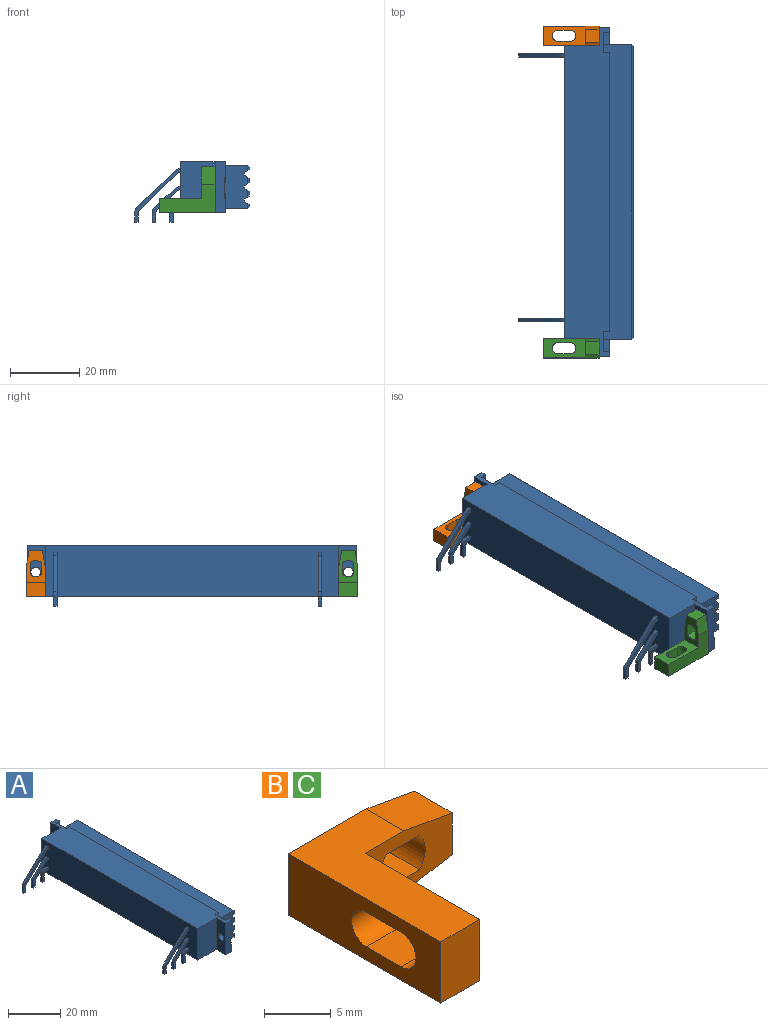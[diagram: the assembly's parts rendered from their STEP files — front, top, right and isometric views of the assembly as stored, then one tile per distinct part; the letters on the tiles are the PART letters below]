
ASSEMBLY  parts=3 mates=6
PART A: 168 faces, bbox 33.1x94.8x17.6 mm
  f0: cylinder r=0.85mm len=1mm, axis (0,-1,0), area 1.3mm2, adj f1,f6,f7,f8
  f1: plane 3.75x1mm, normal (1,0,0), area 3.7mm2, adj f0,f2,f6,f8
  f2: plane 1x1mm, normal (0,0,-1), area 1mm2, adj f1,f3,f6,f8
  f3: plane 3.75x1mm, normal (-1,0,0), area 3.7mm2, adj f2,f4,f6,f8
  f4: cylinder r=1.85mm len=1.85mm, axis (0,-1,0), area 2.9mm2, adj f3,f5,f6,f8
  f5: plane 1.15x1mm, normal (0,0,1), area 1.2mm2, adj f4,f6,f8,f166
  f6: plane 5.6x3mm, normal (0,-1,0), area 7mm2, adj f0,f1,f2,f3,f4,f5,f7,f166
  f7: plane 1.15x1mm, normal (0,0,-1), area 1.2mm2, adj f0,f6,f8,f166
  f8: plane 5.6x3mm, normal (0,1,0), area 7mm2, adj f0,f1,f2,f3,f4,f5,f7,f166
  f9: plane 5.72x5.34mm, normal (0.68,0,-0.73), area 7.8mm2, adj f10,f17,f18,f19
  f10: cylinder r=1mm len=1mm, axis (0,-1,0), area 0.8mm2, adj f9,f11,f17,f19
  f11: plane 2.8x1mm, normal (1,0,0), area 2.8mm2, adj f10,f12,f17,f19
  f12: plane 1x1mm, normal (0,0,-1), area 1mm2, adj f11,f13,f17,f19
  f13: plane 2.8x1mm, normal (-1,0,0), area 2.8mm2, adj f12,f14,f17,f19
  f14: cylinder r=2mm len=1.46mm, axis (0,-1,0), area 1.6mm2, adj f13,f15,f17,f19
  f15: plane 5.72x5.34mm, normal (-0.68,0,0.73), area 7.8mm2, adj f14,f16,f17,f19
  f16: cylinder r=4mm len=1.73mm, axis (0,-1,0), area 2mm2, adj f15,f17,f19,f166
  f17: plane 10.55x8.08mm, normal (0,-1,0), area 13.5mm2, adj f9,f10,f11,f12,f13,f14,f15,f16
  f18: cylinder r=3mm len=1.05mm, axis (0,-1,0), area 1.2mm2, adj f9,f17,f19,f166
  f19: plane 10.55x8.08mm, normal (0,1,0), area 13.5mm2, adj f9,f10,f11,f12,f13,f14,f15,f16
  f20: plane 10.77x10.39mm, normal (0.69,0,-0.72), area 15mm2, adj f21,f28,f29,f30
  f21: cylinder r=1mm len=1mm, axis (0,-1,0), area 0.8mm2, adj f20,f22,f28,f30
  f22: plane 2.8x1mm, normal (1,0,0), area 2.8mm2, adj f21,f23,f28,f30
  f23: plane 1x1mm, normal (0,0,-1), area 1mm2, adj f22,f24,f28,f30
  f24: plane 2.8x1mm, normal (-1,0,0), area 2.8mm2, adj f23,f25,f28,f30
  f25: cylinder r=2mm len=1.44mm, axis (0,-1,0), area 1.6mm2, adj f24,f26,f28,f30
  f26: plane 10.77x10.39mm, normal (-0.69,0,0.72), area 15mm2, adj f25,f27,f28,f30
  f27: cylinder r=4mm len=1.78mm, axis (0,-1,0), area 2.1mm2, adj f26,f28,f30,f166
  f28: plane 15.63x13.16mm, normal (0,-1,0), area 20.6mm2, adj f20,f21,f22,f23,f24,f25,f26,f27
  f29: cylinder r=3mm len=1.08mm, axis (0,-1,0), area 1.3mm2, adj f20,f28,f30,f166
  f30: plane 15.63x13.16mm, normal (0,1,0), area 20.6mm2, adj f20,f21,f22,f23,f24,f25,f26,f27
  f31: cylinder r=0.85mm len=1mm, axis (0,-1,0), area 1.3mm2, adj f32,f37,f38,f39
  f32: plane 3.75x1mm, normal (1,0,0), area 3.7mm2, adj f31,f33,f37,f39
  f33: plane 1x1mm, normal (0,0,-1), area 1mm2, adj f32,f34,f37,f39
  f34: plane 3.75x1mm, normal (-1,0,0), area 3.7mm2, adj f33,f35,f37,f39
  f35: cylinder r=1.85mm len=1.85mm, axis (0,-1,0), area 2.9mm2, adj f34,f36,f37,f39
  f36: plane 1.15x1mm, normal (0,0,1), area 1.1mm2, adj f35,f37,f39,f166
  f37: plane 5.6x3mm, normal (0,-1,0), area 7mm2, adj f31,f32,f33,f34,f35,f36,f38,f166
  f38: plane 1.15x1mm, normal (0,0,-1), area 1.1mm2, adj f31,f37,f39,f166
  f39: plane 5.6x3mm, normal (0,1,0), area 7mm2, adj f31,f32,f33,f34,f35,f36,f38,f166
  f40: plane 5.72x5.34mm, normal (0.68,0,-0.73), area 7.8mm2, adj f41,f48,f49,f50
  f41: cylinder r=1mm len=1mm, axis (0,-1,0), area 0.8mm2, adj f40,f42,f48,f50
  f42: plane 2.8x1mm, normal (1,0,0), area 2.8mm2, adj f41,f43,f48,f50
  f43: plane 1x1mm, normal (0,0,-1), area 1mm2, adj f42,f44,f48,f50
  f44: plane 2.8x1mm, normal (-1,0,0), area 2.8mm2, adj f43,f45,f48,f50
  f45: cylinder r=2mm len=1.46mm, axis (0,-1,0), area 1.6mm2, adj f44,f46,f48,f50
  f46: plane 5.72x5.34mm, normal (-0.68,0,0.73), area 7.8mm2, adj f45,f47,f48,f50
  f47: cylinder r=4mm len=1.73mm, axis (0,-1,0), area 2mm2, adj f46,f48,f50,f166
  f48: plane 10.55x8.08mm, normal (0,-1,0), area 13.5mm2, adj f40,f41,f42,f43,f44,f45,f46,f47
  f49: cylinder r=3mm len=1.05mm, axis (0,-1,0), area 1.2mm2, adj f40,f48,f50,f166
  f50: plane 10.55x8.08mm, normal (0,1,0), area 13.5mm2, adj f40,f41,f42,f43,f44,f45,f46,f47
  f51: cylinder r=1mm len=1mm, axis (0,-1,0), area 0.8mm2, adj f52,f58,f59,f60
  f52: plane 2.8x1mm, normal (1,0,0), area 2.8mm2, adj f51,f53,f58,f60
  f53: plane 1x1mm, normal (0,0,-1), area 1mm2, adj f52,f54,f58,f60
  f54: plane 2.8x1mm, normal (-1,0,0), area 2.8mm2, adj f53,f55,f58,f60
  f55: cylinder r=2mm len=1.44mm, axis (0,-1,0), area 1.6mm2, adj f54,f56,f58,f60
  f56: plane 10.77x10.39mm, normal (-0.69,0,0.72), area 15mm2, adj f55,f57,f58,f60
  f57: cylinder r=4mm len=1.78mm, axis (0,-1,0), area 2.1mm2, adj f56,f58,f60,f166
  f58: plane 15.63x13.16mm, normal (0,-1,0), area 20.6mm2, adj f51,f52,f53,f54,f55,f56,f57,f59
  f59: plane 10.77x10.39mm, normal (0.69,0,-0.72), area 15mm2, adj f51,f58,f60,f167
  f60: plane 15.63x13.16mm, normal (0,1,0), area 20.6mm2, adj f51,f52,f53,f54,f55,f56,f57,f59
  f61: cylinder r=1.4mm len=2.8mm, axis (-1,0,0), area 22.9mm2, adj f63,f157
  f62: plane 14.75x10mm, normal (0,1,0), area 147.5mm2, adj f63,f154,f164,f166
  f63: plane 14.75x5.15mm, normal (-1,0,0), area 69.8mm2, adj f61,f62,f154,f158,f164
  f64: plane 14.75x5.15mm, normal (-1,0,0), area 69.8mm2, adj f65,f143,f154,f164,f165
  f65: cylinder r=1.4mm len=2.8mm, axis (-1,0,0), area 22.9mm2, adj f64,f142
  f66: plane 2.98x1.75mm, normal (0,-1,0), area 5.2mm2, adj f67,f153,f154,f155
  f67: plane 3.45x1.75mm, normal (0,0,1), area 6mm2, adj f66,f129,f153,f155
  f68: plane 2.55x1.47mm, normal (0,0.5,-0.87), area 1.2mm2, adj f129,f155,f156,f157
  f69: plane 3.45x1.75mm, normal (0,0,-1), area 6mm2, adj f129,f161,f162,f163
  f70: plane 2.3x0.8mm, normal (1,0,0), area 1.8mm2, adj f71,f76,f77,f78
  f71: plane 2.3x0.4mm, normal (0,0,1), area 0.9mm2, adj f70,f76,f78,f120
  f72: plane 2.3x0.8mm, normal (1,0,0), area 1.8mm2, adj f73,f74,f121,f122
  f73: plane 2.3x0.4mm, normal (0,0,-1), area 0.9mm2, adj f72,f74,f122,f127
  f74: plane 0.8x0.4mm, normal (0,-1,0), area 0.3mm2, adj f72,f73,f75,f121
  f75: plane 73.9x0.8mm, normal (1,0,0), area 59.1mm2, adj f74,f76,f120,f127
  f76: plane 0.8x0.4mm, normal (0,1,0), area 0.3mm2, adj f70,f71,f75,f77
  f77: plane 2.3x0.4mm, normal (0,0,-1), area 0.9mm2, adj f70,f76,f78,f127
  f78: plane 0.8x0.4mm, normal (0,-1,0), area 0.3mm2, adj f70,f71,f77,f79
  f79: plane 1.93x0.8mm, normal (1,0,0), area 1.5mm2, adj f78,f120,f127,f129
  f80: plane 83.9x1.31mm, normal (1,0,0), area 109.9mm2, adj f81,f118,f119,f120
  f81: plane 1.89x0.5mm, normal (0.71,0.71,0), area 1.1mm2, adj f80,f118,f120,f129
  f82: plane 2.3x0.8mm, normal (1,0,0), area 1.8mm2, adj f83,f88,f89,f90
  f83: plane 2.3x0.4mm, normal (0,0,1), area 0.9mm2, adj f82,f88,f90,f114
  f84: plane 2.3x0.8mm, normal (1,0,0), area 1.8mm2, adj f85,f86,f115,f116
  f85: plane 2.3x0.4mm, normal (0,0,-1), area 0.9mm2, adj f84,f86,f116,f118
  f86: plane 0.8x0.4mm, normal (0,-1,0), area 0.3mm2, adj f84,f85,f87,f115
  f87: plane 73.9x0.8mm, normal (1,0,0), area 59.1mm2, adj f86,f88,f114,f118
  f88: plane 0.8x0.4mm, normal (0,1,0), area 0.3mm2, adj f82,f83,f87,f89
  f89: plane 2.3x0.4mm, normal (0,0,-1), area 0.9mm2, adj f82,f88,f90,f118
  f90: plane 0.8x0.4mm, normal (0,-1,0), area 0.3mm2, adj f82,f83,f89,f91
  f91: plane 1.93x0.8mm, normal (1,0,0), area 1.5mm2, adj f90,f114,f118,f129
  f92: plane 83.9x1.31mm, normal (1,0,0), area 109.9mm2, adj f93,f112,f113,f114
  f93: plane 1.89x0.5mm, normal (0.71,0.71,0), area 1.1mm2, adj f92,f112,f114,f129
  f94: plane 2.3x0.8mm, normal (1,0,0), area 1.8mm2, adj f95,f100,f101,f102
  f95: plane 2.3x0.4mm, normal (0,0,1), area 0.9mm2, adj f94,f100,f102,f108
  f96: plane 2.3x0.8mm, normal (1,0,0), area 1.8mm2, adj f97,f98,f109,f110
  f97: plane 2.3x0.4mm, normal (0,0,-1), area 0.9mm2, adj f96,f98,f110,f112
  f98: plane 0.8x0.4mm, normal (0,-1,0), area 0.3mm2, adj f96,f97,f99,f109
  f99: plane 73.9x0.8mm, normal (1,0,0), area 59.1mm2, adj f98,f100,f108,f112
  f100: plane 0.8x0.4mm, normal (0,1,0), area 0.3mm2, adj f94,f95,f99,f101
  f101: plane 2.3x0.4mm, normal (0,0,-1), area 0.9mm2, adj f94,f100,f102,f112
  f102: plane 0.8x0.4mm, normal (0,-1,0), area 0.3mm2, adj f94,f95,f101,f103
  f103: plane 1.93x0.8mm, normal (1,0,0), area 1.5mm2, adj f102,f108,f112,f129
  f104: plane 83.9x0.64mm, normal (1,0,0), area 53.7mm2, adj f105,f106,f107,f108
  f105: plane 1.43x0.5mm, normal (0.71,0.71,0), area 0.7mm2, adj f104,f106,f108,f129
  f106: plane 84.9x0.5mm, normal (0.71,0,-0.71), area 59.7mm2, adj f104,f105,f107,f130
  f107: plane 1.43x0.5mm, normal (0.71,-0.71,0), area 0.7mm2, adj f104,f106,f108,f141
  f108: plane 84.9x1.47mm, normal (0.5,0,0.87), area 144mm2, adj f95,f99,f103,f104,f105,f107,f109,f111
  f109: plane 2.3x0.4mm, normal (0,0,1), area 0.9mm2, adj f96,f98,f108,f110
  f110: plane 0.8x0.4mm, normal (0,1,0), area 0.3mm2, adj f96,f97,f109,f111
  f111: plane 4.47x0.8mm, normal (1,0,0), area 3.6mm2, adj f108,f110,f112,f141
  f112: plane 84.9x1.47mm, normal (0.5,0,-0.87), area 144mm2, adj f92,f93,f97,f99,f101,f103,f111,f113
  f113: plane 1.89x0.5mm, normal (0.71,-0.71,0), area 1.1mm2, adj f92,f112,f114,f141
  f114: plane 84.9x1.47mm, normal (0.5,0,0.87), area 144mm2, adj f83,f87,f91,f92,f93,f113,f115,f117
  f115: plane 2.3x0.4mm, normal (0,0,1), area 0.9mm2, adj f84,f86,f114,f116
  f116: plane 0.8x0.4mm, normal (0,1,0), area 0.3mm2, adj f84,f85,f115,f117
  f117: plane 4.47x0.8mm, normal (1,0,0), area 3.6mm2, adj f114,f116,f118,f141
  f118: plane 84.9x1.47mm, normal (0.5,0,-0.87), area 144mm2, adj f80,f81,f85,f87,f89,f91,f117,f119
  f119: plane 1.89x0.5mm, normal (0.71,-0.71,0), area 1.1mm2, adj f80,f118,f120,f141
  f120: plane 84.9x1.47mm, normal (0.5,0,0.87), area 144mm2, adj f71,f75,f79,f80,f81,f119,f121,f123
  f121: plane 2.3x0.4mm, normal (0,0,1), area 0.9mm2, adj f72,f74,f120,f122
  f122: plane 0.8x0.4mm, normal (0,1,0), area 0.3mm2, adj f72,f73,f121,f123
  f123: plane 4.47x0.8mm, normal (1,0,0), area 3.6mm2, adj f120,f122,f127,f141
  f124: plane 84.9x0.5mm, normal (0.71,0,0.71), area 59.7mm2, adj f125,f126,f128,f149
  f125: plane 83.9x0.64mm, normal (1,0,0), area 53.7mm2, adj f124,f126,f127,f128
  f126: plane 1.43x0.5mm, normal (0.71,-0.71,0), area 0.7mm2, adj f124,f125,f127,f141
  f127: plane 84.9x1.47mm, normal (0.5,0,-0.87), area 144mm2, adj f73,f75,f77,f79,f123,f125,f126,f128
  f128: plane 1.43x0.5mm, normal (0.71,0.71,0), area 0.7mm2, adj f124,f125,f127,f129
  f129: plane 12.4x8.15mm, normal (0,1,0), area 82.9mm2, adj f67,f68,f69,f79,f81,f91,f93,f103
  f130: plane 84.9x8.15mm, normal (0,0,-1), area 551.1mm2, adj f106,f129,f131,f132,f133,f134,f141,f163
  f131: plane 1.75x1.18mm, normal (0,1,0), area 2.1mm2, adj f130,f132,f163,f164
  f132: plane 80.5x1.18mm, normal (1,0,0), area 94.6mm2, adj f130,f131,f133,f164
  f133: plane 1.75x1.18mm, normal (0,-1,0), area 2.1mm2, adj f130,f132,f134,f164
  f134: plane 5.75x2.98mm, normal (1,0,0), area 13.1mm2, adj f130,f133,f135,f136,f141,f164
  f135: plane 3.55x1.75mm, normal (0,0,-1), area 6.2mm2, adj f134,f136,f138,f141
  f136: plane 2.98x1.75mm, normal (0,1,0), area 5.2mm2, adj f134,f135,f138,f164
  f137: plane 2.4x0.4mm, normal (0,0,1), area 1mm2, adj f138,f139,f142,f143
  f138: plane 5.55x4.95mm, normal (1,0,0), area 11.5mm2, adj f135,f136,f137,f139,f141,f143,f164
  f139: plane 2.55x1.47mm, normal (0,-0.5,0.87), area 1.2mm2, adj f137,f138,f141,f142
  f140: plane 3.55x1.75mm, normal (0,0,1), area 6.2mm2, adj f141,f146,f147,f148
  f141: plane 12.4x8.15mm, normal (0,-1,0), area 82.9mm2, adj f107,f108,f111,f112,f113,f114,f117,f118
  f142: plane 6x4.95mm, normal (1,0,0), area 19.8mm2, adj f65,f137,f139,f141,f143,f144,f145
  f143: plane 14.75x3mm, normal (0,-1,0), area 41.8mm2, adj f64,f137,f138,f142,f144,f146,f154,f164
  f144: plane 2.4x0.4mm, normal (0,0,-1), area 1mm2, adj f142,f143,f145,f146
  f145: plane 2.55x1.47mm, normal (0,-0.5,-0.87), area 1.2mm2, adj f141,f142,f144,f146
  f146: plane 6.15x4.95mm, normal (1,0,0), area 14.5mm2, adj f140,f141,f143,f144,f145,f147,f154
  f147: plane 2.98x1.75mm, normal (0,1,0), area 5.2mm2, adj f140,f146,f148,f154
  f148: plane 5.75x2.98mm, normal (1,0,0), area 13.1mm2, adj f140,f141,f147,f149,f150,f154
  f149: plane 84.9x8.15mm, normal (0,0,1), area 551.1mm2, adj f124,f129,f141,f148,f150,f151,f152,f153
  f150: plane 1.75x1.18mm, normal (0,-1,0), area 2.1mm2, adj f148,f149,f151,f154
  f151: plane 80.5x1.18mm, normal (1,0,0), area 94.6mm2, adj f149,f150,f152,f154
  f152: plane 1.75x1.18mm, normal (0,1,0), area 2.1mm2, adj f149,f151,f153,f154
  f153: plane 5.65x2.98mm, normal (1,0,0), area 12.8mm2, adj f66,f67,f129,f149,f152,f154
  f154: plane 94.8x13mm, normal (0,0,1), area 1109.4mm2, adj f62,f63,f64,f66,f143,f146,f147,f148
  f155: plane 6.15x4.95mm, normal (1,0,0), area 14.8mm2, adj f66,f67,f68,f129,f154,f156,f158
  f156: plane 2.4x0.4mm, normal (0,0,-1), area 1mm2, adj f68,f155,f157,f158
  f157: plane 6x4.95mm, normal (1,0,0), area 19.8mm2, adj f61,f68,f129,f156,f158,f159,f160
  f158: plane 14.75x3mm, normal (0,1,0), area 41.8mm2, adj f63,f154,f155,f156,f157,f159,f161,f164
  f159: plane 2.4x0.4mm, normal (0,0,1), area 1mm2, adj f157,f158,f160,f161
  f160: plane 2.55x1.47mm, normal (0,0.5,0.87), area 1.2mm2, adj f129,f157,f159,f161
  f161: plane 5.55x4.95mm, normal (1,0,0), area 11.8mm2, adj f69,f129,f158,f159,f160,f162,f164
  f162: plane 2.98x1.75mm, normal (0,-1,0), area 5.2mm2, adj f69,f161,f163,f164
  f163: plane 5.65x2.98mm, normal (1,0,0), area 12.8mm2, adj f69,f129,f130,f131,f162,f164
  f164: plane 94.8x13mm, normal (0,0,-1), area 1109.4mm2, adj f62,f63,f64,f131,f132,f133,f134,f136
  f165: plane 14.75x10mm, normal (0,-1,0), area 147.5mm2, adj f64,f154,f164,f166
  f166: plane 84.5x14.75mm, normal (-1,0,0), area 1240.2mm2, adj f5,f6,f7,f8,f16,f17,f18,f19
  f167: cylinder r=3mm len=1.08mm, axis (0,-1,0), area 1.3mm2, adj f58,f59,f60,f166
PART B: 18 faces, bbox 13.3x16.1x5.6 mm
  f0: cylinder r=2.35mm len=4mm, axis (0,-1,0), area 13.8mm2, adj f2,f9,f16,f17
  f1: cylinder r=2.35mm len=4mm, axis (0,-1,0), area 13.8mm2, adj f2,f9,f16,f17
  f2: plane 4x3.49mm, normal (0,0,-1), area 14mm2, adj f0,f1,f9,f16
  f3: plane 4.1x3.65mm, normal (0,0,1), area 15mm2, adj f4,f6,f8,f13
  f4: cylinder r=1.57mm len=4.1mm, axis (-1,0,0), area 20.3mm2, adj f3,f5,f8,f13
  f5: plane 4.1x3.65mm, normal (0,0,-1), area 15mm2, adj f4,f6,f8,f13
  f6: cylinder r=1.57mm len=4.1mm, axis (-1,0,0), area 20.3mm2, adj f3,f5,f8,f13
  f7: plane 5.6x4.1mm, normal (0,-1,0), area 23mm2, adj f8,f12,f13,f14
  f8: plane 16.1x5.6mm, normal (-1,0,0), area 70.9mm2, adj f3,f4,f5,f6,f7,f9,f12,f14
  f9: plane 13.3x5.6mm, normal (0,1,0), area 56.3mm2, adj f0,f1,f2,f8,f10,f11,f12,f14
  f10: plane 4x3.8mm, normal (1,0,0), area 15.2mm2, adj f9,f11,f15,f16
  f11: plane 5.1x4mm, normal (0.17,0,0.98), area 20.7mm2, adj f9,f10,f12,f16
  f12: plane 16.1x8.2mm, normal (0,0,1), area 82.4mm2, adj f7,f8,f9,f11,f13,f16
  f13: plane 12.1x5.6mm, normal (1,0,0), area 48.5mm2, adj f3,f4,f5,f6,f7,f12,f14,f16
  f14: plane 16.1x8.2mm, normal (0,0,-1), area 82.4mm2, adj f7,f8,f9,f13,f15,f16
  f15: plane 5.1x4mm, normal (0.17,0,-0.98), area 20.7mm2, adj f9,f10,f14,f16
  f16: plane 9.2x5.6mm, normal (0,-1,0), area 33.3mm2, adj f0,f1,f2,f10,f11,f12,f13,f14
  f17: plane 4x3.49mm, normal (0,0,1), area 14mm2, adj f0,f1,f9,f16
PART C: same geometry as B
PLACE A at identity fixed
PLACE B rot(axis=(-0.58,-0.58,-0.58),120deg) t=(4.8,5.63,-0.94)mm
PLACE C rot(axis=(-0.58,-0.58,-0.58),120deg) t=(4.8,-84.37,-0.94)mm
MATE planar B.f9 <-> A.f63  axis (1,0,0) through (12.5,5.63,5.9)mm
MATE pin_slot B.f0 <-> A.f61  axis (1,0,0) through (12.5,5.63,8.1)mm
MATE planar C.f9 <-> A.f64  axis (1,0,0) through (12.5,-81.57,4.1)mm
MATE planar C.f8 <-> A.f164  axis (0,0,-1) through (5,-84.37,0)mm
MATE planar A.f164 <-> B.f8  axis (0,0,-1) through (9.04,-39.36,0)mm
MATE pin_slot C.f1 <-> A.f65  axis (1,0,0) through (12.5,-84.37,8.1)mm
